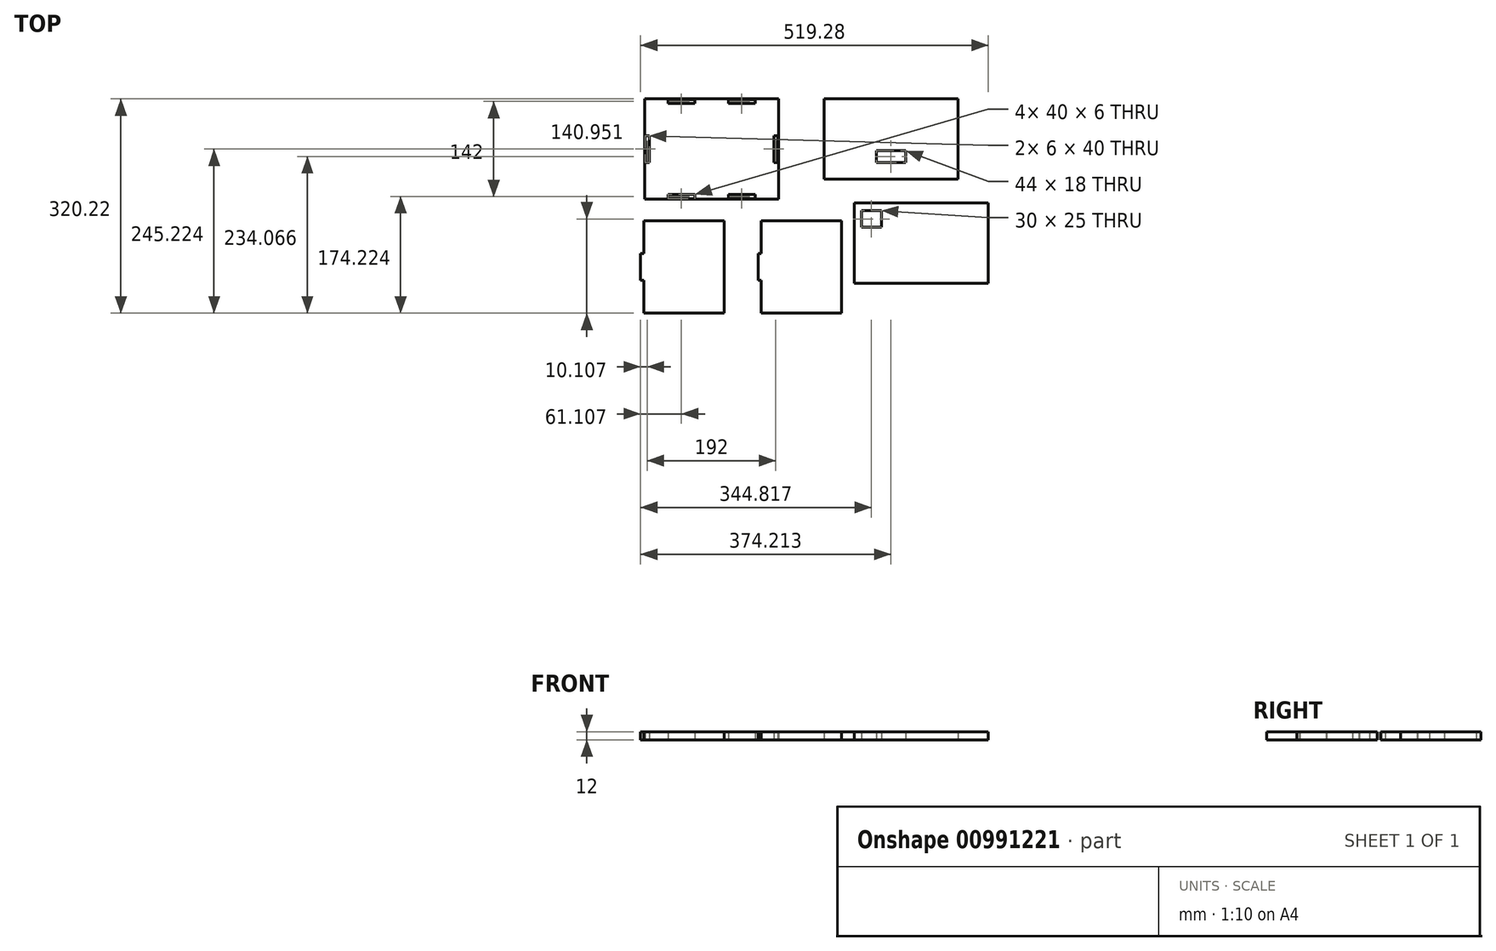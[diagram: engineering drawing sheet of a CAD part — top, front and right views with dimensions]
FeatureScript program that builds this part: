
annotation { "Feature Type Name" : "Feature", "Feature Type Description" : "" }
export const myFeature = defineFeature(function(context is Context, id is Id, definition is map)
    precondition{}
    {
        {
            var Q0;
            Q0=qCreatedBy(makeId("Top.planeOp"),FACE);
            var sketch = newSketch(context, id + "F0", { "sketchPlane" : qUnion([Q0])});
            skLineSegment(sketch, "E0.bottom", {"start": v(-154.4, 123.13) * mm, "end": v(45.6, 123.13) * mm});
            skLineSegment(sketch, "E0.top", {"start": v(-154.4, -26.87) * mm, "end": v(45.6, -26.87) * mm});
            skLineSegment(sketch, "E0.left", {"start": v(-154.4, 123.13) * mm, "end": v(-154.4, -26.87) * mm});
            skLineSegment(sketch, "E0.right", {"start": v(45.6, 123.13) * mm, "end": v(45.6, -26.87) * mm});
            skLineSegment(sketch, "E1.bottom", {"start": v(-153.4, 68.13) * mm, "end": v(-147.4, 68.13) * mm});
            skLineSegment(sketch, "E1.top", {"start": v(-153.4, 28.13) * mm, "end": v(-147.4, 28.13) * mm});
            skLineSegment(sketch, "E1.left", {"start": v(-153.4, 68.13) * mm, "end": v(-153.4, 28.13) * mm});
            skLineSegment(sketch, "E1.right", {"start": v(-147.4, 68.13) * mm, "end": v(-147.4, 28.13) * mm});
            skLineSegment(sketch, "E2.bottom", {"start": v(-119.4, 122.13) * mm, "end": v(-79.4, 122.13) * mm});
            skLineSegment(sketch, "E2.top", {"start": v(-119.4, 116.13) * mm, "end": v(-79.4, 116.13) * mm});
            skLineSegment(sketch, "E2.left", {"start": v(-119.4, 122.13) * mm, "end": v(-119.4, 116.13) * mm});
            skLineSegment(sketch, "E2.right", {"start": v(-79.4, 122.13) * mm, "end": v(-79.4, 116.13) * mm});
            skLineSegment(sketch, "E3.bottom", {"start": v(38.6, 68.13) * mm, "end": v(44.6, 68.13) * mm});
            skLineSegment(sketch, "E3.top", {"start": v(38.6, 28.13) * mm, "end": v(44.6, 28.13) * mm});
            skLineSegment(sketch, "E3.left", {"start": v(38.6, 68.13) * mm, "end": v(38.6, 28.13) * mm});
            skLineSegment(sketch, "E3.right", {"start": v(44.6, 68.13) * mm, "end": v(44.6, 28.13) * mm});
            skLineSegment(sketch, "E4.bottom", {"start": v(-29.4, 122.13) * mm, "end": v(10.6, 122.13) * mm});
            skLineSegment(sketch, "E4.top", {"start": v(-29.4, 116.13) * mm, "end": v(10.6, 116.13) * mm});
            skLineSegment(sketch, "E4.left", {"start": v(-29.4, 122.13) * mm, "end": v(-29.4, 116.13) * mm});
            skLineSegment(sketch, "E4.right", {"start": v(10.6, 122.13) * mm, "end": v(10.6, 116.13) * mm});
            skLineSegment(sketch, "E5.bottom", {"start": v(-119.4, -19.87) * mm, "end": v(-79.4, -19.87) * mm});
            skLineSegment(sketch, "E5.top", {"start": v(-119.4, -25.87) * mm, "end": v(-79.4, -25.87) * mm});
            skLineSegment(sketch, "E5.left", {"start": v(-119.4, -19.87) * mm, "end": v(-119.4, -25.87) * mm});
            skLineSegment(sketch, "E5.right", {"start": v(-79.4, -19.87) * mm, "end": v(-79.4, -25.87) * mm});
            skLineSegment(sketch, "E6.bottom", {"start": v(-29.4, -19.87) * mm, "end": v(10.6, -19.87) * mm});
            skLineSegment(sketch, "E6.top", {"start": v(-29.4, -25.87) * mm, "end": v(10.6, -25.87) * mm});
            skLineSegment(sketch, "E6.left", {"start": v(-29.4, -19.87) * mm, "end": v(-29.4, -25.87) * mm});
            skLineSegment(sketch, "E6.right", {"start": v(10.6, -19.87) * mm, "end": v(10.6, -25.87) * mm});
            skPoint(sketch, "E7.firstSnap0", {"position": v(-54.4, 123.13) * mm});
            skLineSegment(sketch, "E7.bottom", {"start": v(113.7, 123.13) * mm, "end": v(313.7, 123.13) * mm});
            skLineSegment(sketch, "E7.top", {"start": v(113.7, 3.13) * mm, "end": v(313.7, 3.13) * mm});
            skLineSegment(sketch, "E7.left", {"start": v(113.7, 123.13) * mm, "end": v(113.7, 3.13) * mm});
            skLineSegment(sketch, "E7.right", {"start": v(313.7, 123.13) * mm, "end": v(313.7, 3.13) * mm});
            skLineSegment(sketch, "E8.bottom", {"start": v(149.2, 123.13) * mm, "end": v(188.2, 123.13) * mm});
            skLineSegment(sketch, "E8.top", {"start": v(149.2, 128.13) * mm, "end": v(188.2, 128.13) * mm});
            skLineSegment(sketch, "E8.left", {"start": v(149.2, 128.13) * mm, "end": v(149.2, 123.13) * mm});
            skLineSegment(sketch, "E8.right", {"start": v(188.2, 128.13) * mm, "end": v(188.2, 123.13) * mm});
            skLineSegment(sketch, "E9.bottom", {"start": v(239.2, 123.13) * mm, "end": v(278.2, 123.13) * mm});
            skLineSegment(sketch, "E9.top", {"start": v(239.2, 128.13) * mm, "end": v(278.2, 128.13) * mm});
            skLineSegment(sketch, "E9.left", {"start": v(239.2, 128.13) * mm, "end": v(239.2, 123.13) * mm});
            skLineSegment(sketch, "E9.right", {"start": v(278.2, 128.13) * mm, "end": v(278.2, 123.13) * mm});
            skLineSegment(sketch, "E10.bottom", {"start": v(158.77, -32.15) * mm, "end": v(358.77, -32.15) * mm});
            skLineSegment(sketch, "E10.top", {"start": v(158.77, -152.15) * mm, "end": v(358.77, -152.15) * mm});
            skLineSegment(sketch, "E10.left", {"start": v(158.77, -32.15) * mm, "end": v(158.77, -152.15) * mm});
            skLineSegment(sketch, "E10.right", {"start": v(358.77, -32.15) * mm, "end": v(358.77, -152.15) * mm});
            skLineSegment(sketch, "E11.bottom", {"start": v(193.77, -32.15) * mm, "end": v(232.77, -32.15) * mm});
            skLineSegment(sketch, "E11.top", {"start": v(193.77, -27.15) * mm, "end": v(232.77, -27.15) * mm});
            skLineSegment(sketch, "E11.left", {"start": v(193.77, -27.15) * mm, "end": v(193.77, -32.15) * mm});
            skLineSegment(sketch, "E11.right", {"start": v(232.77, -27.15) * mm, "end": v(232.77, -32.15) * mm});
            skLineSegment(sketch, "E12.bottom", {"start": v(284.77, -32.15) * mm, "end": v(323.77, -32.15) * mm});
            skLineSegment(sketch, "E12.top", {"start": v(284.77, -27.15) * mm, "end": v(323.77, -27.15) * mm});
            skLineSegment(sketch, "E12.left", {"start": v(284.77, -27.15) * mm, "end": v(284.77, -32.15) * mm});
            skLineSegment(sketch, "E12.right", {"start": v(323.77, -27.15) * mm, "end": v(323.77, -32.15) * mm});
            skLineSegment(sketch, "E13.bottom", {"start": v(191.7, 45.98) * mm, "end": v(235.7, 45.98) * mm});
            skLineSegment(sketch, "E13.top", {"start": v(191.7, 27.98) * mm, "end": v(235.7, 27.98) * mm});
            skLineSegment(sketch, "E13.left", {"start": v(191.7, 45.98) * mm, "end": v(191.7, 27.98) * mm});
            skLineSegment(sketch, "E13.right", {"start": v(235.7, 45.98) * mm, "end": v(235.7, 27.98) * mm});
            skLineSegment(sketch, "E14.bottom", {"start": v(-155.51, -58.68) * mm, "end": v(-35.51, -58.68) * mm});
            skLineSegment(sketch, "E14.top", {"start": v(-155.51, -196.68) * mm, "end": v(-35.51, -196.68) * mm});
            skLineSegment(sketch, "E14.left", {"start": v(-155.51, -58.68) * mm, "end": v(-155.51, -196.68) * mm});
            skLineSegment(sketch, "E14.right", {"start": v(-35.51, -58.68) * mm, "end": v(-35.51, -196.68) * mm});
            skLineSegment(sketch, "E15.bottom", {"start": v(-160.51, -107.68) * mm, "end": v(-155.51, -107.68) * mm});
            skLineSegment(sketch, "E15.top", {"start": v(-160.51, -147.68) * mm, "end": v(-155.51, -147.68) * mm});
            skLineSegment(sketch, "E15.left", {"start": v(-160.51, -107.68) * mm, "end": v(-160.51, -147.68) * mm});
            skLineSegment(sketch, "E15.right", {"start": v(-155.51, -107.68) * mm, "end": v(-155.51, -147.68) * mm});
            skLineSegment(sketch, "E16.bottom", {"start": v(19.98, -59.09) * mm, "end": v(139.98, -59.09) * mm});
            skLineSegment(sketch, "E16.top", {"start": v(19.98, -197.09) * mm, "end": v(139.98, -197.09) * mm});
            skLineSegment(sketch, "E16.left", {"start": v(19.98, -59.09) * mm, "end": v(19.98, -197.09) * mm});
            skLineSegment(sketch, "E16.right", {"start": v(139.98, -59.09) * mm, "end": v(139.98, -197.09) * mm});
            skLineSegment(sketch, "E17.bottom", {"start": v(14.98, -108.09) * mm, "end": v(19.98, -108.09) * mm});
            skLineSegment(sketch, "E17.top", {"start": v(14.98, -148.09) * mm, "end": v(19.98, -148.09) * mm});
            skLineSegment(sketch, "E17.left", {"start": v(14.98, -108.09) * mm, "end": v(14.98, -148.09) * mm});
            skLineSegment(sketch, "E17.right", {"start": v(19.98, -108.09) * mm, "end": v(19.98, -148.09) * mm});
            skLineSegment(sketch, "E18.bottom", {"start": v(169.3, -43.64) * mm, "end": v(199.3, -43.64) * mm});
            skLineSegment(sketch, "E18.top", {"start": v(169.3, -68.64) * mm, "end": v(199.3, -68.64) * mm});
            skLineSegment(sketch, "E18.left", {"start": v(169.3, -43.64) * mm, "end": v(169.3, -68.64) * mm});
            skLineSegment(sketch, "E18.right", {"start": v(199.3, -43.64) * mm, "end": v(199.3, -68.64) * mm});
            skSolve(sketch);
        }
        {
            var Q0;
            {var subQ3=sQuery(id+"F0.wireOp",EDGE,"E14.bottom");Q0=makeQuery(id+"F0.imprint","IMPRINT",FACE,{"disambiguationData":[TD([[makeQuery(id+"F0.imprint","IMPRINT",EDGE,{"derivedFrom":subQ3}),-1.0]])]});}
            var Q1;
            Q1=makeQuery(id+"F0.imprint","IMPRINT",FACE,{"disambiguationData":[TD([[makeQuery(id+"F0.imprint","IMPRINT",EDGE,{"derivedFrom":sQuery(id+"F0.wireOp",EDGE,"E0.bottom")}),-1.0]])]});
            var Q2;
            Q2=makeQuery(id+"F0.imprint","IMPRINT",FACE,{"disambiguationData":[TD([[makeQuery(id+"F0.imprint","IMPRINT",EDGE,{"derivedFrom":sQuery(id+"F0.wireOp",EDGE,"E15.bottom")}),-1.0]])]});
            var Q3;
            Q3=makeQuery(id+"F0.imprint","IMPRINT",FACE,{"disambiguationData":[TD([[makeQuery(id+"F0.imprint","IMPRINT",EDGE,{"derivedFrom":sQuery(id+"F0.wireOp",EDGE,"E10.top")}),1.0]])]});
            var Q4;
            Q4=makeQuery(id+"F0.imprint","IMPRINT",FACE,{"disambiguationData":[TD([[makeQuery(id+"F0.imprint","IMPRINT",EDGE,{"derivedFrom":sQuery(id+"F0.wireOp",EDGE,"E7.top")}),1.0]])]});
            var Q5;
            {var subQ3=sQuery(id+"F0.wireOp",EDGE,"E16.bottom");Q5=makeQuery(id+"F0.imprint","IMPRINT",FACE,{"disambiguationData":[TD([[makeQuery(id+"F0.imprint","IMPRINT",EDGE,{"derivedFrom":subQ3}),-1.0]])]});}
            var Q6;
            Q6=makeQuery(id+"F0.imprint","IMPRINT",FACE,{"disambiguationData":[TD([[makeQuery(id+"F0.imprint","IMPRINT",EDGE,{"derivedFrom":sQuery(id+"F0.wireOp",EDGE,"E17.bottom")}),-1.0]])]});
            var Q7;
            Q7=makeQuery(id+"F0.imprint","IMPRINT",FACE,{"disambiguationData":[TD([[makeQuery(id+"F0.imprint","IMPRINT",EDGE,{"derivedFrom":sQuery(id+"F0.wireOp",EDGE,"E12.bottom")}),1.0]])]});
            var Q8;
            Q8=makeQuery(id+"F0.imprint","IMPRINT",FACE,{"disambiguationData":[TD([[makeQuery(id+"F0.imprint","IMPRINT",EDGE,{"derivedFrom":sQuery(id+"F0.wireOp",EDGE,"E11.bottom")}),1.0]])]});
            var Q9;
            Q9=makeQuery(id+"F0.imprint","IMPRINT",FACE,{"disambiguationData":[TD([[makeQuery(id+"F0.imprint","IMPRINT",EDGE,{"derivedFrom":sQuery(id+"F0.wireOp",EDGE,"E8.bottom")}),1.0]])]});
            var Q10;
            Q10=makeQuery(id+"F0.imprint","IMPRINT",FACE,{"disambiguationData":[TD([[makeQuery(id+"F0.imprint","IMPRINT",EDGE,{"derivedFrom":sQuery(id+"F0.wireOp",EDGE,"E9.bottom")}),1.0]])]});
            extrude(context, id + "F1", {"entities" : qUnion([Q0, Q1, Q2, Q3, Q4, Q5, Q6, Q7, Q8, Q9, Q10]), "depth" : 12 * mm, "offsetDistance" : 25 * mm});
        }
    });
